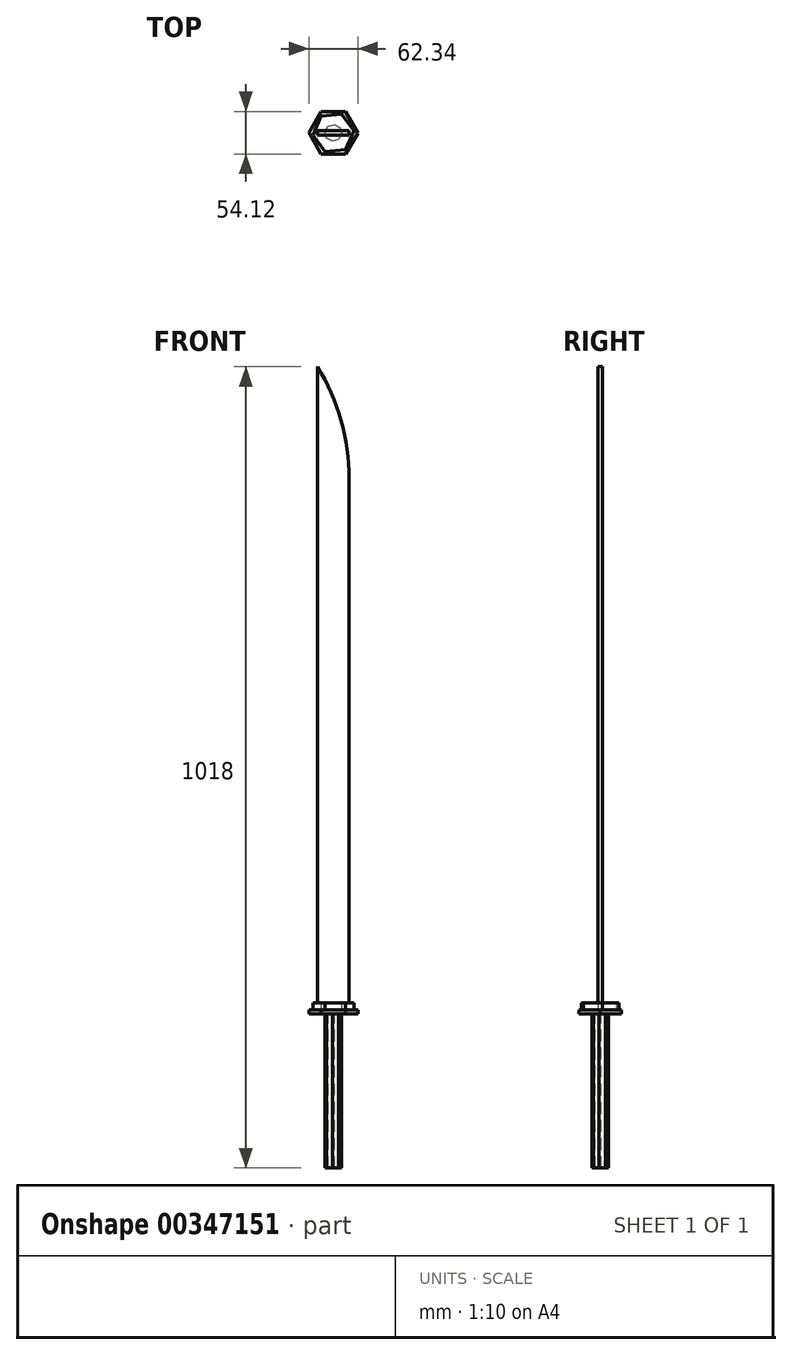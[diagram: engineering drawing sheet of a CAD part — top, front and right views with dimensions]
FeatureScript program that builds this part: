
annotation { "Feature Type Name" : "Feature", "Feature Type Description" : "" }
export const myFeature = defineFeature(function(context is Context, id is Id, definition is map)
    precondition{}
    {
        {
            var Q0;
            Q0=qCreatedBy(makeId("Top.planeOp"),FACE);
            var sketch = newSketch(context, id + "F0", { "sketchPlane" : qUnion([Q0])});
            skLineSegment(sketch, "E0.bottom", {"start": v(56.92, 4.85) * mm, "end": v(-56.92, 4.85) * mm});
            skLineSegment(sketch, "E0.top", {"start": v(56.92, -4.85) * mm, "end": v(-56.92, -4.85) * mm});
            skLineSegment(sketch, "E0.left", {"start": v(56.92, 4.85) * mm, "end": v(56.92, -4.85) * mm});
            skLineSegment(sketch, "E0.right", {"start": v(-56.92, 4.85) * mm, "end": v(-56.92, -4.85) * mm});
            skPoint(sketch, "E0.middle", {"position": v(0, 0) * mm});
            skLineSegment(sketch, "E1.bottom", {"start": v(20.15, -2.99) * mm, "end": v(-20.15, -2.99) * mm});
            skLineSegment(sketch, "E1.top", {"start": v(20.15, 2.99) * mm, "end": v(-20.15, 2.99) * mm});
            skLineSegment(sketch, "E1.left", {"start": v(20.15, -2.99) * mm, "end": v(20.15, 2.99) * mm});
            skLineSegment(sketch, "E1.right", {"start": v(-20.15, -2.99) * mm, "end": v(-20.15, 2.99) * mm});
            skSolve(sketch);
        }
        {
            var Q0;
            Q0=makeQuery(id+"F0.imprint","IMPRINT",FACE,{"disambiguationData":[TD([[makeQuery(id+"F0.imprint","IMPRINT",EDGE,{"derivedFrom":sQuery(id+"F0.wireOp",EDGE,"E1.bottom")}),-1.0]])]});
            extrude(context, id + "F1", {"entities" : qUnion([Q0]), "depth" : 822 * mm});
        }
        {
            var Q0;
            Q0=qCreatedBy(makeId("Top.planeOp"),FACE);
            var sketch = newSketch(context, id + "F2", { "sketchPlane" : qUnion([Q0])});
            skCircle(sketch, "E2.cCircle", {"center": v(0, 0) * mm, "radius": 9.86 * mm, "construction": true});
            skLineSegment(sketch, "E2.0", {"start": v(10.6, -1.3) * mm, "end": v(6.57, -8.4) * mm});
            skLineSegment(sketch, "E2.1", {"start": v(6.57, -8.4) * mm, "end": v(-1.3, -10.6) * mm});
            skLineSegment(sketch, "E2.2", {"start": v(-1.3, -10.6) * mm, "end": v(-8.4, -6.57) * mm});
            skLineSegment(sketch, "E2.3", {"start": v(-8.4, -6.57) * mm, "end": v(-10.6, 1.3) * mm});
            skLineSegment(sketch, "E2.4", {"start": v(-10.6, 1.3) * mm, "end": v(-6.57, 8.4) * mm});
            skLineSegment(sketch, "E2.5", {"start": v(-6.57, 8.4) * mm, "end": v(1.3, 10.6) * mm});
            skLineSegment(sketch, "E2.6", {"start": v(1.3, 10.6) * mm, "end": v(8.4, 6.57) * mm});
            skLineSegment(sketch, "E2.7", {"start": v(8.4, 6.57) * mm, "end": v(10.6, -1.3) * mm});
            skPoint(sketch, "E2.0.midPoint", {"position": v(8.58, -4.85) * mm});
            skSolve(sketch);
        }
        {
            var Q0;
            Q0=makeQuery(id+"F2.imprint","IMPRINT",FACE,{"disambiguationData":[TD([[makeQuery(id+"F2.imprint","IMPRINT",EDGE,{"derivedFrom":sQuery(id+"F2.wireOp",EDGE,"E2.0")}),-1.0]])]});
            extrude(context, id + "F3", {"entities" : qUnion([Q0]), "operationType" : NewBodyOperationType.ADD, "oppositeDirection" : true, "depth" : 196 * mm});
        }
        {
            var Q0;
            Q0=qCreatedBy(makeId("Top.planeOp"),FACE);
            var sketch = newSketch(context, id + "F4", { "sketchPlane" : qUnion([Q0])});
            skCircle(sketch, "E3.cCircle", {"center": v(0, 0) * mm, "radius": 27 * mm, "construction": true});
            skLineSegment(sketch, "E3.0", {"start": v(15.7, 26.93) * mm, "end": v(31.17, -0.14) * mm});
            skLineSegment(sketch, "E3.1", {"start": v(31.17, -0.14) * mm, "end": v(15.47, -27.06) * mm});
            skLineSegment(sketch, "E3.2", {"start": v(15.47, -27.06) * mm, "end": v(-15.7, -26.93) * mm});
            skLineSegment(sketch, "E3.3", {"start": v(-15.7, -26.93) * mm, "end": v(-31.17, 0.14) * mm});
            skLineSegment(sketch, "E3.4", {"start": v(-31.17, 0.14) * mm, "end": v(-15.47, 27.06) * mm});
            skLineSegment(sketch, "E3.5", {"start": v(-15.47, 27.06) * mm, "end": v(15.7, 26.93) * mm});
            skPoint(sketch, "E3.0.midPoint", {"position": v(23.44, 13.4) * mm});
            skSolve(sketch);
        }
        {
            var Q0;
            Q0=makeQuery(id+"F4.imprint","IMPRINT",FACE,{"disambiguationData":[TD([[makeQuery(id+"F4.imprint","IMPRINT",EDGE,{"derivedFrom":sQuery(id+"F4.wireOp",EDGE,"E3.0")}),-1.0]])]});
            extrude(context, id + "F5", {"entities" : qUnion([Q0]), "operationType" : NewBodyOperationType.ADD, "depth" : 5 * mm});
        }
        {
            var Q0;
            Q0=makeQuery(id+"F1.opExtrude","CAP_EDGE",EDGE,{"disambiguationData":[OSD([sQuery(id+"F0.wireOp",EDGE,"E1.left")])],"isStart":false});
            fillet(context, id + "F6", {"entities" : qUnion([Q0]), "radius" : 270.4 * mm, "tangentPropagation" : true, "allowEdgeOverflow" : false});
        }
        {
            var Q0;
            {var subQ5=sQuery(id+"F0.wireOp",EDGE,"E1.top");var subQ7=sQuery(id+"F0.wireOp",EDGE,"E1.right");var subQ8=sQuery(id+"F0.wireOp",EDGE,"E1.bottom");var subQ10=sQuery(id+"F0.wireOp",EDGE,"E1.left");var subQ11=makeQuery(id+"F1.opExtrude","CAP_FACE",FACE,{"disambiguationData":[OSD([subQ8,subQ5,subQ10,subQ7])],"isStart":true});Q0=makeQuery(id+"F5.boolean.opBoolean","MERGE",FACE,{"derivedFrom":[makeQuery(id+"F3.boolean.opBoolean","SPLIT",FACE,{"disambiguationData":[TD([makeQuery(id+"F1.opExtrude","SWEPT_FACE",FACE,{"disambiguationData":[OSD([subQ10])]})])],"derivedFrom":subQ11}),makeQuery(id+"F3.boolean.opBoolean","SPLIT",FACE,{"disambiguationData":[TD([makeQuery(id+"F1.opExtrude","SWEPT_FACE",FACE,{"disambiguationData":[OSD([subQ7])]})])],"derivedFrom":subQ11}),makeQuery(id+"F5.opExtrude","CAP_FACE",FACE,{"disambiguationData":[OSD([sQuery(id+"F4.wireOp",EDGE,"E3.0"),sQuery(id+"F4.wireOp",EDGE,"E3.1"),sQuery(id+"F4.wireOp",EDGE,"E3.2"),sQuery(id+"F4.wireOp",EDGE,"E3.3"),sQuery(id+"F4.wireOp",EDGE,"E3.4"),sQuery(id+"F4.wireOp",EDGE,"E3.5")])],"isStart":true})]});}
            var sketch = newSketch(context, id + "F7", { "sketchPlane" : qUnion([Q0])});
            skCircle(sketch, "E4.cCircle", {"center": v(0, 0) * mm, "radius": 22.6 * mm, "construction": true});
            skLineSegment(sketch, "E4.0", {"start": v(-25.94, 2.82) * mm, "end": v(-10.53, 23.88) * mm});
            skLineSegment(sketch, "E4.1", {"start": v(-10.53, 23.88) * mm, "end": v(15.41, 21.06) * mm});
            skLineSegment(sketch, "E4.2", {"start": v(15.41, 21.06) * mm, "end": v(25.94, -2.82) * mm});
            skLineSegment(sketch, "E4.3", {"start": v(25.94, -2.82) * mm, "end": v(10.53, -23.88) * mm});
            skLineSegment(sketch, "E4.4", {"start": v(10.53, -23.88) * mm, "end": v(-15.41, -21.06) * mm});
            skLineSegment(sketch, "E4.5", {"start": v(-15.41, -21.06) * mm, "end": v(-25.94, 2.82) * mm});
            skPoint(sketch, "E4.0.midPoint", {"position": v(-18.24, 13.35) * mm});
            skSolve(sketch);
        }
        {
            var Q0;
            Q0 = qSketchRegion(id + "F7", true);
            extrude(context, id + "F8", {"entities" : qUnion([Q0]), "operationType" : NewBodyOperationType.ADD, "oppositeDirection" : true, "depth" : 14 * mm, "offsetDistance" : 25 * mm});
        }
    });
